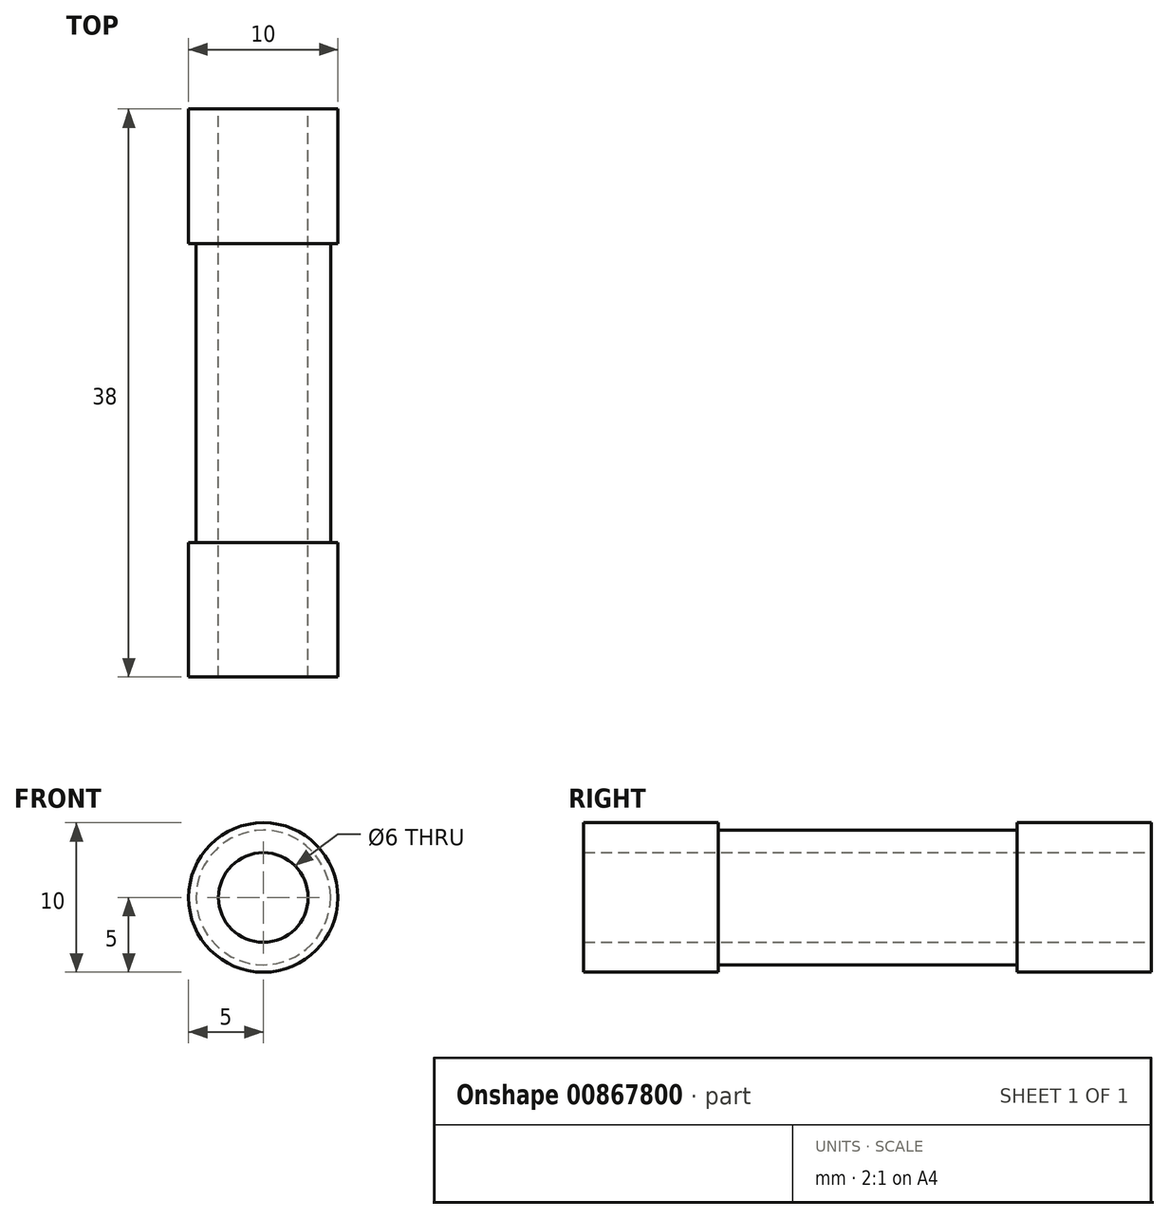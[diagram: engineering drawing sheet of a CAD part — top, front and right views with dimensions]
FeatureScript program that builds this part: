
annotation { "Feature Type Name" : "Feature", "Feature Type Description" : "" }
export const myFeature = defineFeature(function(context is Context, id is Id, definition is map)
    precondition{}
    {
        {
            var Q0;
            Q0=qCreatedBy(makeId("Front.planeOp"),FACE);
            var sketch = newSketch(context, id + "F0", { "sketchPlane" : qUnion([Q0])});
            skCircle(sketch, "E0", {"center": v(0, 0) * mm, "radius": 5 * mm});
            skSolve(sketch);
        }
        {
            var Q0;
            Q0=makeQuery(id+"F0.imprint","IMPRINT",FACE,{"disambiguationData":[TD([[makeQuery(id+"F0.imprint","IMPRINT",EDGE,{"derivedFrom":sQuery(id+"F0.wireOp",EDGE,"E0")}),1.0]])]});
            var sketch = newSketch(context, id + "F1", { "sketchPlane" : qUnion([Q0])});
            skCircle(sketch, "E1", {"center": v(0, 0) * mm, "radius": 4.5 * mm});
            skSolve(sketch);
        }
        {
            var Q0;
            Q0 = qSketchRegion(id + "F0", true);
            extrude(context, id + "F2", {"entities" : qUnion([Q0]), "depth" : 9 * mm, "offsetDistance" : 25.4 * mm});
        }
        {
            var Q0;
            Q0 = qSketchRegion(id + "F1", true);
            extrude(context, id + "F3", {"entities" : qUnion([Q0]), "operationType" : NewBodyOperationType.ADD, "depth" : 19 * mm, "offsetDistance" : 25.4 * mm});
        }
        {
            var Q0;
            Q0=makeQuery(id+"F3.opExtrude","CAP_FACE",FACE,{"disambiguationData":[OSD([sQuery(id+"F1.wireOp",EDGE,"E1")])],"isStart":false});
            cPlane(context, id + "F4", {"entities" : qUnion([Q0]), "cplaneType" : CPlaneType.OFFSET, "offset" : 0 * mm, "width" : 152.4 * mm, "height" : 152.4 * mm});
        }
        {
            var Q0;
            Q0=makeQuery(id+"F2.opExtrude","SWEPT_BODY",BODY,{"disambiguationData":[OSD([sQuery(id+"F0.wireOp",EDGE,"E0")])]});
            var Q1;
            Q1=qCreatedBy(id+"F4.planeOp",FACE);
            mirror(context, id + "F5", {"operationType" : NewBodyOperationType.ADD, "entities" : qUnion([Q0]), "mirrorPlane" : qUnion([Q1])});
        }
        {
            var Q0;
            Q0=makeQuery(id+"F2.opExtrude","CAP_FACE",FACE,{"disambiguationData":[OSD([sQuery(id+"F0.wireOp",EDGE,"E0")])],"isStart":true});
            var sketch = newSketch(context, id + "F6", { "sketchPlane" : qUnion([Q0])});
            skCircle(sketch, "E2", {"center": v(0, 0) * mm, "radius": 3 * mm});
            skSolve(sketch);
        }
        {
            var Q0;
            Q0=makeQuery(id+"F6.imprint","IMPRINT",FACE,{"disambiguationData":[TD([[makeQuery(id+"F6.imprint","IMPRINT",EDGE,{"derivedFrom":sQuery(id+"F6.wireOp",EDGE,"E2")}),1.0]])]});
            extrude(context, id + "F7", {"entities" : qUnion([Q0]), "operationType" : NewBodyOperationType.REMOVE, "oppositeDirection" : true, "depth" : 38 * mm, "offsetDistance" : 25.4 * mm});
        }
    });
